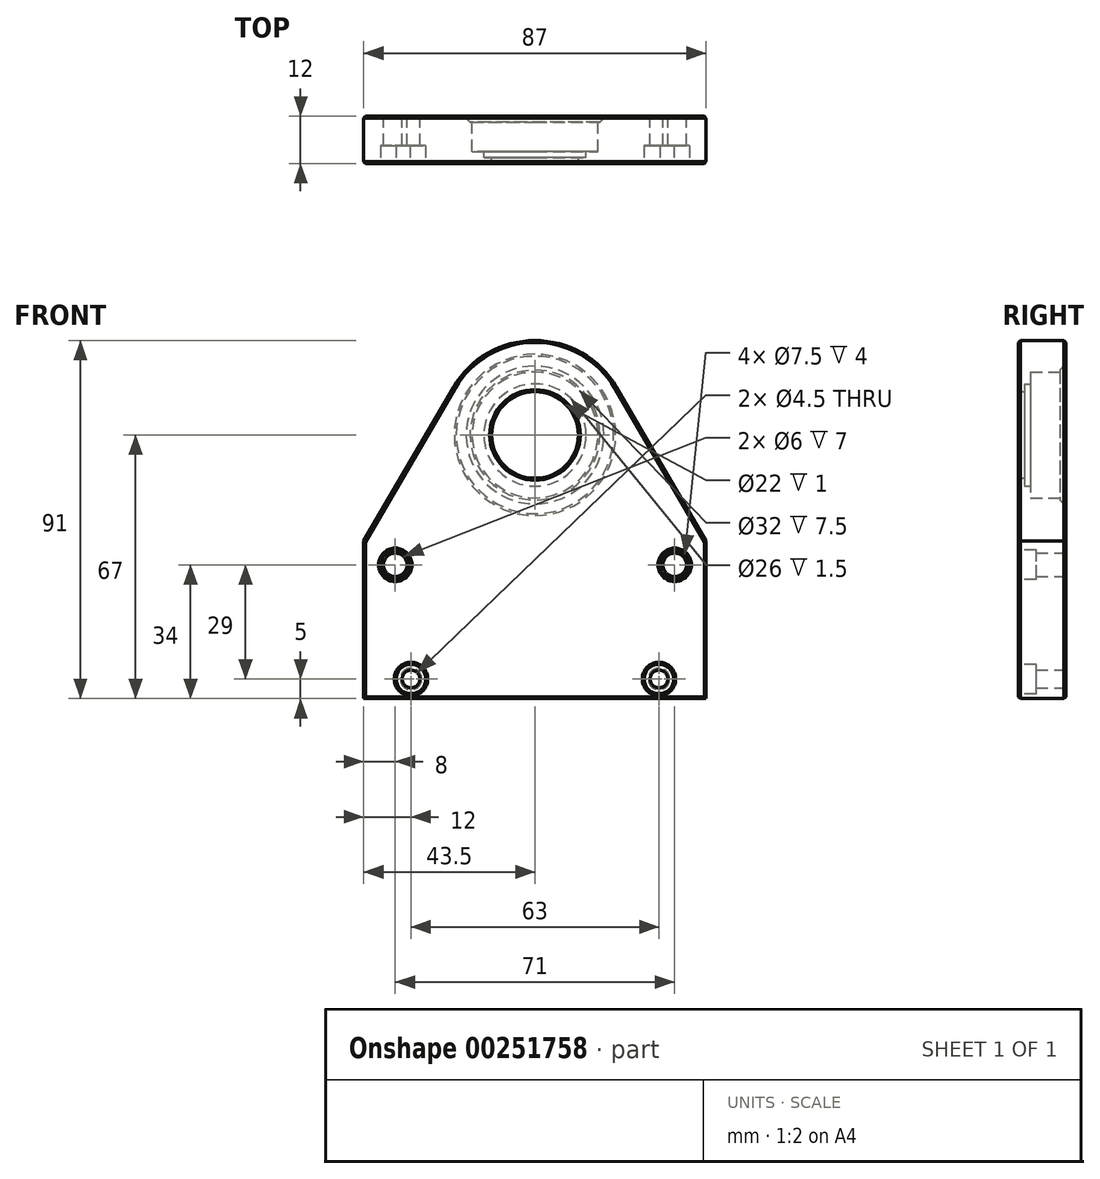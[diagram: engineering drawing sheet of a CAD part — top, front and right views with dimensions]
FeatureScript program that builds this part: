
annotation { "Feature Type Name" : "Feature", "Feature Type Description" : "" }
export const myFeature = defineFeature(function(context is Context, id is Id, definition is map)
    precondition{}
    {
        {
            var Q0;
            Q0=qCreatedBy(makeId("Front.planeOp"),FACE);
            var sketch = newSketch(context, id + "F0", { "sketchPlane" : qUnion([Q0])});
            skLineSegment(sketch, "E0.bottom", {"start": v(43.5, -20) * mm, "end": v(-43.5, -20) * mm});
            skLineSegment(sketch, "E0.top", {"start": v(43.5, 20) * mm, "end": v(-43.5, 20) * mm});
            skLineSegment(sketch, "E0.left", {"start": v(43.5, -20) * mm, "end": v(43.5, 20) * mm});
            skLineSegment(sketch, "E0.right", {"start": v(-43.5, -20) * mm, "end": v(-43.5, 20) * mm});
            skPoint(sketch, "E0.middle", {"position": v(0, 0) * mm});
            skPoint(sketch, "E1", {"position": v(0, 47) * mm});
            skCircle(sketch, "E2", {"center": v(0, 47) * mm, "radius": 11 * mm});
            skArc(sketch, "E3", {"start": v(20.74, 59.08) * mm, "mid": v(0, 71) * mm, "end": v(-20.74, 59.08) * mm});
            skLineSegment(sketch, "E4", {"start": v(-43.5, 20) * mm, "end": v(-20.74, 59.08) * mm});
            skLineSegment(sketch, "E5", {"start": v(43.5, 20) * mm, "end": v(20.74, 59.08) * mm});
            skCircle(sketch, "E6", {"center": v(-35.5, 14) * mm, "radius": 3.75 * mm});
            skCircle(sketch, "E7", {"center": v(-35.5, 14) * mm, "radius": 3 * mm});
            skCircle(sketch, "E8", {"center": v(35.5, 14) * mm, "radius": 3.75 * mm});
            skCircle(sketch, "E9", {"center": v(35.5, 14) * mm, "radius": 3 * mm});
            skCircle(sketch, "E10", {"center": v(-31.5, -15) * mm, "radius": 3.75 * mm});
            skCircle(sketch, "E11", {"center": v(-31.5, -15) * mm, "radius": 2.25 * mm});
            skCircle(sketch, "E12", {"center": v(31.5, -15) * mm, "radius": 3.75 * mm});
            skCircle(sketch, "E13", {"center": v(31.5, -15) * mm, "radius": 2.25 * mm});
            skSolve(sketch);
        }
        {
            var Q0;
            Q0=makeQuery(id+"F0.imprint","IMPRINT",FACE,{"disambiguationData":[TD([[makeQuery(id+"F0.imprint","IMPRINT",EDGE,{"derivedFrom":sQuery(id+"F0.wireOp",EDGE,"E0.top")}),-1.0]])]});
            var Q1;
            Q1=makeQuery(id+"F0.imprint","IMPRINT",FACE,{"disambiguationData":[TD([[makeQuery(id+"F0.imprint","IMPRINT",EDGE,{"derivedFrom":sQuery(id+"F0.wireOp",EDGE,"E0.bottom")}),-1.0]])]});
            var Q2;
            Q2=makeQuery(id+"F0.imprint","IMPRINT",FACE,{"disambiguationData":[TD([[makeQuery(id+"F0.imprint","IMPRINT",EDGE,{"derivedFrom":sQuery(id+"F0.wireOp",EDGE,"E6")}),1.0]])]});
            var Q3;
            Q3=makeQuery(id+"F0.imprint","IMPRINT",FACE,{"disambiguationData":[TD([[makeQuery(id+"F0.imprint","IMPRINT",EDGE,{"derivedFrom":sQuery(id+"F0.wireOp",EDGE,"E10")}),1.0]])]});
            var Q4;
            Q4=makeQuery(id+"F0.imprint","IMPRINT",FACE,{"disambiguationData":[TD([[makeQuery(id+"F0.imprint","IMPRINT",EDGE,{"derivedFrom":sQuery(id+"F0.wireOp",EDGE,"E8")}),1.0]])]});
            var Q5;
            Q5=makeQuery(id+"F0.imprint","IMPRINT",FACE,{"disambiguationData":[TD([[makeQuery(id+"F0.imprint","IMPRINT",EDGE,{"derivedFrom":sQuery(id+"F0.wireOp",EDGE,"E12")}),1.0]])]});
            extrude(context, id + "F1", {"entities" : qUnion([Q0, Q1, Q2, Q3, Q4, Q5]), "depth" : 12 * mm});
        }
        {
            var Q0;
            Q0=makeQuery(id+"F1.opExtrude","CAP_FACE",FACE,{"disambiguationData":[OSD([sQuery(id+"F0.wireOp",EDGE,"E0.bottom"),sQuery(id+"F0.wireOp",EDGE,"E0.left"),sQuery(id+"F0.wireOp",EDGE,"E0.right"),sQuery(id+"F0.wireOp",EDGE,"E2"),sQuery(id+"F0.wireOp",EDGE,"E3"),sQuery(id+"F0.wireOp",EDGE,"E4"),sQuery(id+"F0.wireOp",EDGE,"E5"),sQuery(id+"F0.wireOp",EDGE,"E7"),sQuery(id+"F0.wireOp",EDGE,"E9"),sQuery(id+"F0.wireOp",EDGE,"E11"),sQuery(id+"F0.wireOp",EDGE,"E13")])],"isStart":false});
            var sketch = newSketch(context, id + "F2", { "sketchPlane" : qUnion([Q0])});
            skCircle(sketch, "E14.0", {"center": v(-35.5, 14) * mm, "radius": 3.75 * mm});
            skCircle(sketch, "E15.0", {"center": v(35.5, 14) * mm, "radius": 3.75 * mm});
            skCircle(sketch, "E16.0", {"center": v(-31.5, -15) * mm, "radius": 3.75 * mm});
            skCircle(sketch, "E17.0", {"center": v(31.5, -15) * mm, "radius": 3.75 * mm});
            skCircle(sketch, "E18.0", {"center": v(-35.5, 14) * mm, "radius": 3 * mm});
            skCircle(sketch, "E19.0", {"center": v(-31.5, -15) * mm, "radius": 2.25 * mm});
            skCircle(sketch, "E20.0", {"center": v(31.5, -15) * mm, "radius": 2.25 * mm});
            skCircle(sketch, "E21.0", {"center": v(35.5, 14) * mm, "radius": 3 * mm});
            skSolve(sketch);
        }
        {
            var Q0;
            Q0=makeQuery(id+"F2.imprint","IMPRINT",FACE,{"disambiguationData":[TD([[makeQuery(id+"F2.imprint","IMPRINT",EDGE,{"derivedFrom":sQuery(id+"F2.wireOp",EDGE,"E14.0")}),1.0]])]});
            var Q1;
            Q1=makeQuery(id+"F2.imprint","IMPRINT",FACE,{"disambiguationData":[TD([[makeQuery(id+"F2.imprint","IMPRINT",EDGE,{"derivedFrom":sQuery(id+"F2.wireOp",EDGE,"E15.0")}),1.0]])]});
            var Q2;
            Q2=makeQuery(id+"F2.imprint","IMPRINT",FACE,{"disambiguationData":[TD([[makeQuery(id+"F2.imprint","IMPRINT",EDGE,{"derivedFrom":sQuery(id+"F2.wireOp",EDGE,"E16.0")}),1.0]])]});
            var Q3;
            Q3=makeQuery(id+"F2.imprint","IMPRINT",FACE,{"disambiguationData":[TD([[makeQuery(id+"F2.imprint","IMPRINT",EDGE,{"derivedFrom":sQuery(id+"F2.wireOp",EDGE,"E17.0")}),1.0]])]});
            extrude(context, id + "F3", {"entities" : qUnion([Q0, Q1, Q2, Q3]), "operationType" : NewBodyOperationType.REMOVE, "oppositeDirection" : true, "depth" : 4.5 * mm});
        }
        {
            var Q0;
            Q0=makeQuery(id+"F1.opExtrude","CAP_FACE",FACE,{"disambiguationData":[OSD([sQuery(id+"F0.wireOp",EDGE,"E0.bottom"),sQuery(id+"F0.wireOp",EDGE,"E0.left"),sQuery(id+"F0.wireOp",EDGE,"E0.right"),sQuery(id+"F0.wireOp",EDGE,"E2"),sQuery(id+"F0.wireOp",EDGE,"E3"),sQuery(id+"F0.wireOp",EDGE,"E4"),sQuery(id+"F0.wireOp",EDGE,"E5"),sQuery(id+"F0.wireOp",EDGE,"E7"),sQuery(id+"F0.wireOp",EDGE,"E9"),sQuery(id+"F0.wireOp",EDGE,"E11"),sQuery(id+"F0.wireOp",EDGE,"E13")])],"isStart":true});
            var sketch = newSketch(context, id + "F4", { "sketchPlane" : qUnion([Q0])});
            skCircle(sketch, "E22", {"center": v(0, 47) * mm, "radius": 20 * mm});
            skSolve(sketch);
        }
        {
            var Q0;
            Q0 = qSketchRegion(id + "F4", true);
            extrude(context, id + "F5", {"entities" : qUnion([Q0]), "operationType" : NewBodyOperationType.REMOVE, "oppositeDirection" : true, "depth" : .5 * mm});
        }
        {
            var Q0;
            Q0=makeQuery(id+"F1.opExtrude","CAP_FACE",FACE,{"disambiguationData":[OSD([sQuery(id+"F0.wireOp",EDGE,"E0.bottom"),sQuery(id+"F0.wireOp",EDGE,"E0.left"),sQuery(id+"F0.wireOp",EDGE,"E0.right"),sQuery(id+"F0.wireOp",EDGE,"E2"),sQuery(id+"F0.wireOp",EDGE,"E3"),sQuery(id+"F0.wireOp",EDGE,"E4"),sQuery(id+"F0.wireOp",EDGE,"E5"),sQuery(id+"F0.wireOp",EDGE,"E7"),sQuery(id+"F0.wireOp",EDGE,"E9"),sQuery(id+"F0.wireOp",EDGE,"E11"),sQuery(id+"F0.wireOp",EDGE,"E13")])],"isStart":true});
            var sketch = newSketch(context, id + "F6", { "sketchPlane" : qUnion([Q0])});
            skCircle(sketch, "E23", {"center": v(0, 47) * mm, "radius": 16.5 * mm});
            skSolve(sketch);
        }
        {
            var Q0;
            Q0 = qSketchRegion(id + "F6", true);
            extrude(context, id + "F7", {"entities" : qUnion([Q0]), "operationType" : NewBodyOperationType.REMOVE, "oppositeDirection" : true, "depth" : 1.5 * mm});
        }
        {
            var Q0;
            Q0=makeQuery(id+"F1.opExtrude","CAP_FACE",FACE,{"disambiguationData":[OSD([sQuery(id+"F0.wireOp",EDGE,"E0.bottom"),sQuery(id+"F0.wireOp",EDGE,"E0.left"),sQuery(id+"F0.wireOp",EDGE,"E0.right"),sQuery(id+"F0.wireOp",EDGE,"E2"),sQuery(id+"F0.wireOp",EDGE,"E3"),sQuery(id+"F0.wireOp",EDGE,"E4"),sQuery(id+"F0.wireOp",EDGE,"E5"),sQuery(id+"F0.wireOp",EDGE,"E7"),sQuery(id+"F0.wireOp",EDGE,"E9"),sQuery(id+"F0.wireOp",EDGE,"E11"),sQuery(id+"F0.wireOp",EDGE,"E13")])],"isStart":true});
            var sketch = newSketch(context, id + "F8", { "sketchPlane" : qUnion([Q0])});
            skCircle(sketch, "E24", {"center": v(0, 47) * mm, "radius": 16 * mm});
            skSolve(sketch);
        }
        {
            var Q0;
            Q0 = qSketchRegion(id + "F8", true);
            extrude(context, id + "F9", {"entities" : qUnion([Q0]), "operationType" : NewBodyOperationType.REMOVE, "oppositeDirection" : true, "depth" : 9 * mm});
        }
        {
            var Q0;
            Q0=makeQuery(id+"F1.opExtrude","CAP_FACE",FACE,{"disambiguationData":[OSD([sQuery(id+"F0.wireOp",EDGE,"E0.bottom"),sQuery(id+"F0.wireOp",EDGE,"E0.left"),sQuery(id+"F0.wireOp",EDGE,"E0.right"),sQuery(id+"F0.wireOp",EDGE,"E2"),sQuery(id+"F0.wireOp",EDGE,"E3"),sQuery(id+"F0.wireOp",EDGE,"E4"),sQuery(id+"F0.wireOp",EDGE,"E5"),sQuery(id+"F0.wireOp",EDGE,"E7"),sQuery(id+"F0.wireOp",EDGE,"E9"),sQuery(id+"F0.wireOp",EDGE,"E11"),sQuery(id+"F0.wireOp",EDGE,"E13")])],"isStart":true});
            var sketch = newSketch(context, id + "F10", { "sketchPlane" : qUnion([Q0])});
            skCircle(sketch, "E25", {"center": v(0, 47) * mm, "radius": 13 * mm});
            skSolve(sketch);
        }
        {
            var Q0;
            Q0 = qSketchRegion(id + "F10", true);
            extrude(context, id + "F11", {"entities" : qUnion([Q0]), "operationType" : NewBodyOperationType.REMOVE, "oppositeDirection" : true, "depth" : 10.5 * mm});
        }
        {
            var Q0;
            Q0=makeQuery(id+"F1.opExtrude","CAP_FACE",FACE,{"disambiguationData":[OSD([sQuery(id+"F0.wireOp",EDGE,"E0.bottom"),sQuery(id+"F0.wireOp",EDGE,"E0.left"),sQuery(id+"F0.wireOp",EDGE,"E0.right"),sQuery(id+"F0.wireOp",EDGE,"E2"),sQuery(id+"F0.wireOp",EDGE,"E3"),sQuery(id+"F0.wireOp",EDGE,"E4"),sQuery(id+"F0.wireOp",EDGE,"E5"),sQuery(id+"F0.wireOp",EDGE,"E7"),sQuery(id+"F0.wireOp",EDGE,"E9"),sQuery(id+"F0.wireOp",EDGE,"E11"),sQuery(id+"F0.wireOp",EDGE,"E13")])],"isStart":false});
            chamfer(context, id + "F12", {"entities" : qUnion([Q0]), "chamferType" : ChamferType.OFFSET_ANGLE, "width" : .5 * mm, "oppositeDirection" : false, "angle" : 45 * degree, "tangentPropagation" : true});
        }
        {
            var Q0;
            Q0=makeQuery(id+"F1.opExtrude","CAP_FACE",FACE,{"disambiguationData":[OSD([sQuery(id+"F0.wireOp",EDGE,"E0.bottom"),sQuery(id+"F0.wireOp",EDGE,"E0.left"),sQuery(id+"F0.wireOp",EDGE,"E0.right"),sQuery(id+"F0.wireOp",EDGE,"E2"),sQuery(id+"F0.wireOp",EDGE,"E3"),sQuery(id+"F0.wireOp",EDGE,"E4"),sQuery(id+"F0.wireOp",EDGE,"E5"),sQuery(id+"F0.wireOp",EDGE,"E7"),sQuery(id+"F0.wireOp",EDGE,"E9"),sQuery(id+"F0.wireOp",EDGE,"E11"),sQuery(id+"F0.wireOp",EDGE,"E13")])],"isStart":true});
            chamfer(context, id + "F13", {"entities" : qUnion([Q0]), "chamferType" : ChamferType.OFFSET_ANGLE, "width" : .5 * mm, "oppositeDirection" : false, "angle" : 45 * degree, "tangentPropagation" : true});
        }
        {
            var Q0;
            Q0=makeQuery(id+"F7.boolean.opBoolean","INTERSECT",EDGE,{"derivedFrom":[makeQuery(id+"F5.boolean.opBoolean","COPY",FACE,{"derivedFrom":makeQuery(id+"F5.opExtrude","CAP_FACE",FACE,{"disambiguationData":[OSD([sQuery(id+"F4.wireOp",EDGE,"E22")])],"isStart":false})}),makeQuery(id+"F7.opExtrude","SWEPT_FACE",FACE,{"disambiguationData":[OSD([sQuery(id+"F6.wireOp",EDGE,"E23")])]})]});
            chamfer(context, id + "F14", {"entities" : qUnion([Q0]), "chamferType" : ChamferType.OFFSET_ANGLE, "width" : (1) * mm, "oppositeDirection" : false, "angle" : 45 * degree, "tangentPropagation" : true});
        }
    });
